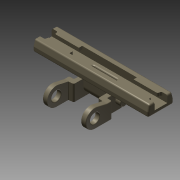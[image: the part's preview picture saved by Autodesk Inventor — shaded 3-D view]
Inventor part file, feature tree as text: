
AUTODESK INVENTOR PART (.ipt)
format: ipt  version: 2013 (Build 170138000, 138)  size: 529,408 bytes
history: native  units: in
note: dims shown in document units (in); Inventor stores cm internally (conversion verified against a paired STEP export)
features: fillet x13, sketch x12, extrude x11, plane x8, mirror x3, projected_geometry x2, hole x1
ambient origin geometry x8: Origin, YZ Plane, XZ Plane, XY Plane, X Axis, Y Axis, Z Axis, Center Point
bodies: Solid1 (feature_tree)
feature tree (50):
  extrude  "Extrusion1"  Depth=0.3268in
  plane  "Work Plane1"
  fillet  "Fillet1"  Radius=0.061in
  extrude  "Extrusion2"  Depth=0.244in
  plane  "Work Plane2"
  extrude  "Extrusion4"  Depth=0.224in
  plane  "Work Plane3"
  extrude  "Extrusion7"  Depth=0.0591in TaperAngle=0.0deg
  extrude  "Extrusion9"  Depth=0.0021in
  fillet  "Fillet5"  Radius=0.1634in
  fillet  "Fillet6"  Radius=0.0453in
  fillet  "Fillet7"  Radius=0.1634in
  hole  "Hole1"  [1 undecoded]
  fillet  "Fillet8"  Radius=0.6205in
  fillet  "Fillet9"  Radius=0.0984in
  plane  "Work Plane4"
  mirror  "Mirror1"
  fillet  "Fillet10"  Radius=0.1181in
  extrude  "Extrusion11"  Depth=0.063in TaperAngle=0.0deg
  extrude  "Extrusion12"  Depth=0.0079in
  plane  "Work Plane7"
  extrude  "Extrusion13"  Depth=0.0079in
  fillet  "Fillet12"  Radius=0.0079in
  mirror  "Mirror2"
  extrude  "Extrusion14"  Depth=0.0197in
  fillet  "Fillet14"  Radius=0.258in
  fillet  "Fillet15"  Radius=0.1181in
  plane  "Work Plane8"
  fillet  "Fillet17"  Radius=0.0669in
  fillet  "Fillet18"  Radius=0.0392in
  extrude  "Extrusion20"  Depth=0.008in
  extrude  "Extrusion21"  Depth=0.0197in
  mirror  "Mirror4"
  fillet  "Fillet20"  Radius=1.0625in
  sketch  "Sketch1"  dims[d0=1.4961in d1=0.3268in d2=0.061in d3=0.0in]
  sketch  "Sketch2"  dims[d5=0.315in d6=0.0in d10=0.244in]
  sketch  "Sketch6"  dims[d11=0.2362in d12=0.224in]
  sketch  "Sketch10"  dims[d13=0.087in d15=0.0591in d16=0.0in]
  sketch  "Sketch11"  dims[d17=0.063in d27=0.0021in d28=0.1634in d29=0.0453in d30=0.1634in]
  sketch  "Sketch13"  dims[d31=0.126in d32=0.6205in d33=0.6205in d34=0.0984in d35=0.1181in]
  plane  "Work Plane5"
  plane  "Work Plane6"
  sketch  "Sketch15"  dims[d38=0.3858in d39=0.063in d40=0.0591in d41=0.0in d42=0.0in]
  sketch  "Sketch16"  dims[d49=0.063in d50=0.0in d51=0.0079in d52=0.02in]
  sketch  "Sketch17"  dims[d53=0.0079in d54=0.0079in]
  sketch  "Sketch18"  dims[d55=0.122in d56=0.75in d57=0.375in d58=0.25in d59=0.5635in d60=1.0in d61=0.8108in d62=0.0079in]
  projected_geometry  "Projected Loop3"
  projected_geometry  "Projected Loop4"
  sketch  "Sketch22"  dims[d63=0.0787in d64=0.0197in d69=0.258in d70=-0.0034in d72=0.1181in d73=0.0669in d74=0.0in d75=0.0392in]
  sketch  "Sketch23"  dims[d76=0.066in d77=0.0in d78=0.008in d79=0.0197in d80=1.0625in d81=0.0in d86=0.0591in d87=0.126in d89=0.122in d101=0.315in d102=1.1404in d103=1.1404in d104=0.1378in d109=0.0197in d110=0.0197in d117=0.0118in d119=0.1654in d120=0.0906in d123=0.1063in d124=0.0in d125=0.0394in d126=0.0in d127=0.0197in]
note: 1 required parameter value undecoded (feature->parameter linkage not recoverable at this tier; creation-order binding heuristic only, values carry confidence <= 0.55)
